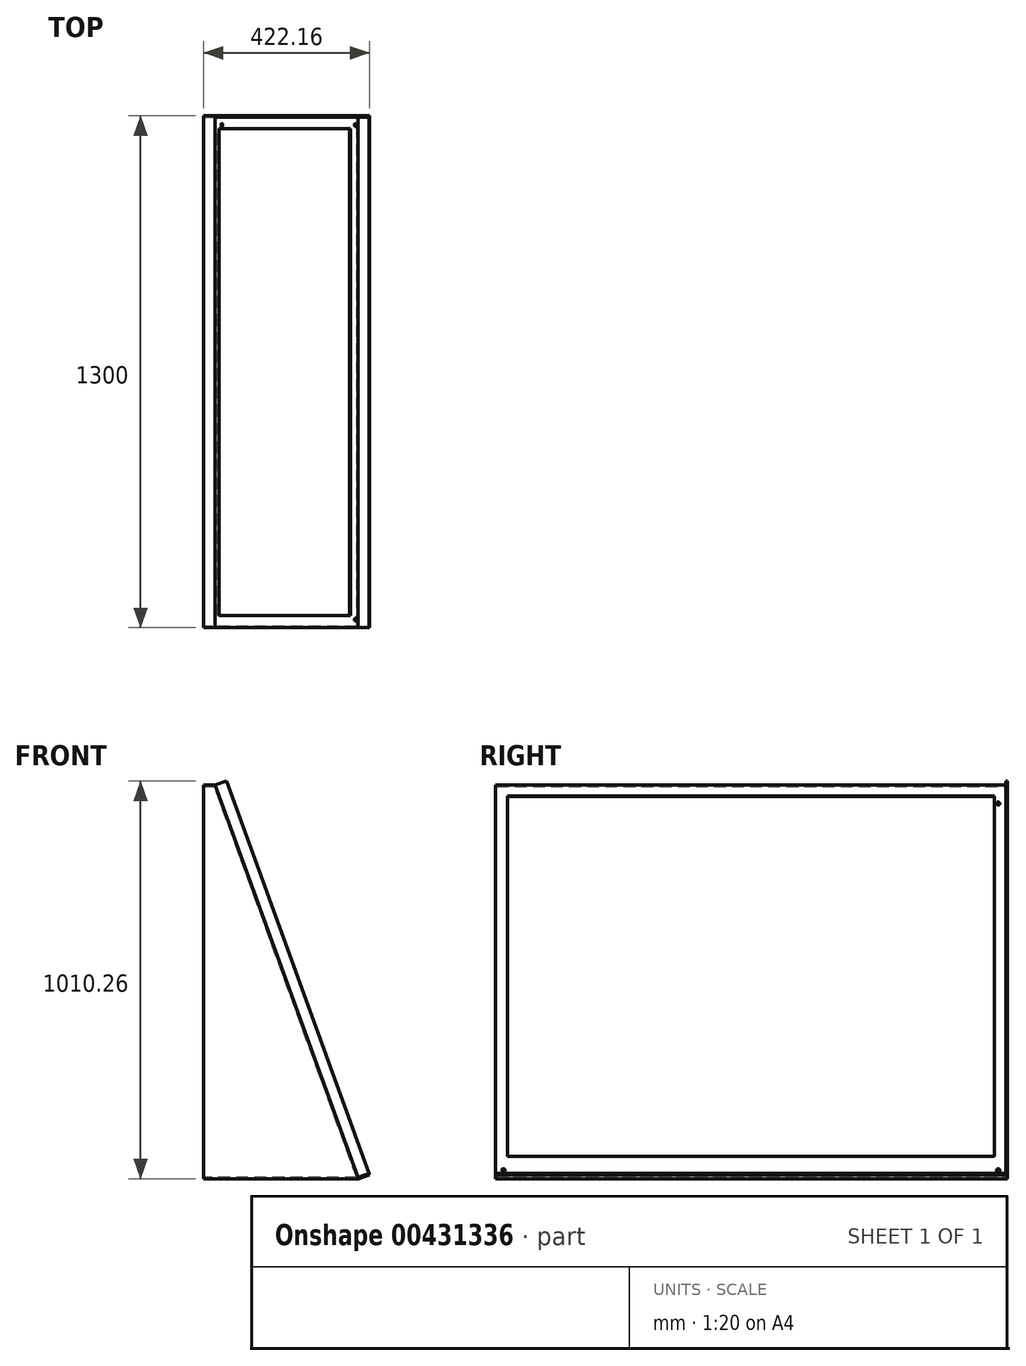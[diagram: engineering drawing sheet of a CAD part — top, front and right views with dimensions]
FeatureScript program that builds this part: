
annotation { "Feature Type Name" : "Feature", "Feature Type Description" : "" }
export const myFeature = defineFeature(function(context is Context, id is Id, definition is map)
    precondition{}
    {
        {
            var Q0;
            Q0=qCreatedBy(makeId("Front.planeOp"),FACE);
            var sketch = newSketch(context, id + "F0", { "sketchPlane" : qUnion([Q0])});
            skLineSegment(sketch, "E0", {"start": v(0, 0) * mm, "end": v(-393.97, 0) * mm});
            skLineSegment(sketch, "E1", {"start": v(-393.97, 0) * mm, "end": v(-393.97, 1000) * mm});
            skLineSegment(sketch, "E2", {"start": v(-393.97, 1000) * mm, "end": v(-363.97, 1000) * mm});
            skLineSegment(sketch, "E3", {"start": v(-1.03, 2.82) * mm, "end": v(-363.97, 1000) * mm});
            skLineSegment(sketch, "E4", {"start": v(0, 0) * mm, "end": v(28.2, 10.26) * mm});
            skLineSegment(sketch, "E5", {"start": v(28.2, 10.26) * mm, "end": v(27.16, 13.08) * mm});
            skLineSegment(sketch, "E6", {"start": v(27.16, 13.08) * mm, "end": v(-1.03, 2.82) * mm});
            skSolve(sketch);
        }
        {
            var Q0;
            Q0=makeQuery(id+"F0.imprint","IMPRINT",FACE,{"disambiguationData":[TD([[makeQuery(id+"F0.imprint","IMPRINT",EDGE,{"derivedFrom":sQuery(id+"F0.wireOp",EDGE,"E0")}),-1.0]])]});
            extrude(context, id + "F1", {"entities" : qUnion([Q0]), "endBound" : BoundingType.SYMMETRIC, "depth" : 1300 * mm});
        }
        {
            var Q0;
            Q0=makeQuery(id+"F1.opExtrude","SWEPT_FACE",FACE,{"disambiguationData":[OSD([sQuery(id+"F0.wireOp",EDGE,"E1")])]});
            shell(context, id + "F2", {"entities" : qUnion([Q0]), "thickness" : 3 * mm});
        }
        {
            var Q0;
            Q0=makeQuery(id+"F1.opExtrude","SWEPT_FACE",FACE,{"disambiguationData":[OSD([sQuery(id+"F0.wireOp",EDGE,"E3")])]});
            var sketch = newSketch(context, id + "F3", { "sketchPlane" : qUnion([Q0])});
            skLineSegment(sketch, "E7.bottom", {"start": v(-620, 1034.18) * mm, "end": v(617, 1034.18) * mm});
            skLineSegment(sketch, "E7.top", {"start": v(-620, 60) * mm, "end": v(617, 60) * mm});
            skLineSegment(sketch, "E7.left", {"start": v(-620, 1034.18) * mm, "end": v(-620, 60) * mm});
            skLineSegment(sketch, "E7.right", {"start": v(617, 1034.18) * mm, "end": v(617, 60) * mm});
            skSolve(sketch);
        }
        {
            var Q0;
            Q0 = qSketchRegion(id + "F3", true);
            extrude(context, id + "F4", {"entities" : qUnion([Q0]), "operationType" : NewBodyOperationType.REMOVE, "oppositeDirection" : true, "depth" : 3 * mm});
        }
        {
            var Q0;
            Q0=makeQuery(id+"F1.opExtrude","SWEPT_FACE",FACE,{"disambiguationData":[OSD([sQuery(id+"F0.wireOp",EDGE,"E3")])]});
            var sketch = newSketch(context, id + "F5", { "sketchPlane" : qUnion([Q0])});
            skLineSegment(sketch, "E8.bottom", {"start": v(650, 3) * mm, "end": v(647, 3) * mm});
            skLineSegment(sketch, "E8.top", {"start": v(650, 1064.18) * mm, "end": v(647, 1064.18) * mm});
            skLineSegment(sketch, "E8.left", {"start": v(650, 3) * mm, "end": v(650, 1064.18) * mm});
            skLineSegment(sketch, "E8.right", {"start": v(647, 3) * mm, "end": v(647, 1064.18) * mm});
            skSolve(sketch);
        }
        {
            var Q0;
            Q0 = qSketchRegion(id + "F5", true);
            extrude(context, id + "F6", {"entities" : qUnion([Q0]), "operationType" : NewBodyOperationType.ADD, "depth" : 30 * mm});
        }
        {
            var Q0;
            Q0=makeQuery(id+"F1.opExtrude","SWEPT_FACE",FACE,{"disambiguationData":[OSD([sQuery(id+"F0.wireOp",EDGE,"E3")])]});
            var sketch = newSketch(context, id + "F7", { "sketchPlane" : qUnion([Q0])});
            skCircle(sketch, "E9", {"center": v(627, 23) * mm, "radius": 4 * mm});
            skCircle(sketch, "E10", {"center": v(-630, 23) * mm, "radius": 4 * mm});
            skCircle(sketch, "E11", {"center": v(627, 1014.18) * mm, "radius": 4 * mm});
            skSolve(sketch);
        }
        {
            var Q0;
            Q0 = qSketchRegion(id + "F7", true);
            extrude(context, id + "F8", {"entities" : qUnion([Q0]), "operationType" : NewBodyOperationType.REMOVE, "oppositeDirection" : true, "depth" : 25 * mm});
        }
    });
